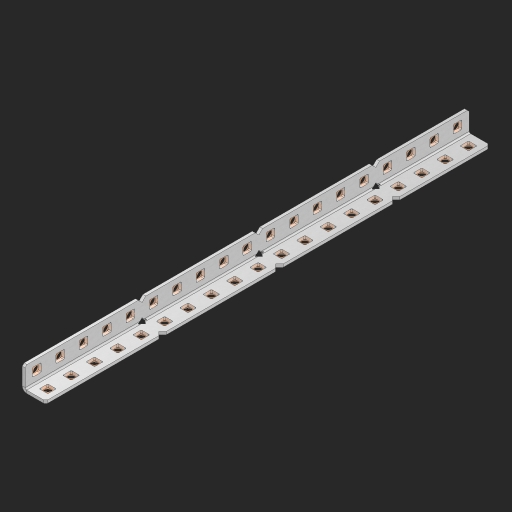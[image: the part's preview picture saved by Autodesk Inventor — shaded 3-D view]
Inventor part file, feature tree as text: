
AUTODESK INVENTOR PART (.ipt)
format: ipt  version: 2023 (Build 270158000, 158)  size: 778,752 bytes
history: native  units: in
note: dims shown in document units (in); Inventor stores cm internally (conversion verified against a paired STEP export)
features: other x44, extrude x39, sheet_metal_op x8, sketch x5, pattern_linear x1, mirror x1, chamfer x1
ambient origin geometry x8: Origin, YZ Plane, XZ Plane, XY Plane, X Axis, Y Axis, Z Axis, Center Point
bodies: Solid1 (feature_tree), Body (feature_tree)
feature tree (99):
  sheet_metal_op  "Flanges"
  sheet_metal_op  "Body Pattern"
  other  "Arc Length"
  pattern_linear  "Notch Pattern"  Spacing1=0.125in  [1 undecoded]
  other  "Diagonal Plane"
  mirror  "Everything Mirrored"
  chamfer  "End Chamfer"
  sketch  "Sketch1"  dims[d0=0.5in]
  other  "Plate1"
  sketch  "Sketch2"  dims[d1=9.5in]
  other  "Plate2"
  sheet_metal_op  "Bend1"
  sheet_metal_op  "Corner1"
  sketch  "Sketch8"  dims[d2=0.0625in]
  sketch  "Sketch9"  dims[d3=0.0625in]
  other  "Srf91"
  sheet_metal_op  "Body Pattern Sketch"
  other  "Srf92"
  sketch  "Sketch13"  dims[d4=0.0312in d5=0.125in d6=0.0625in d7=0.5in d8=90.0deg d9=0.0312in d10=0.25in d11=0.0625in d12=0.0625in d49=0.182in d50=0.02in d52=0.25in d53=0.0625in d54=0.0in d55=0.172in d56=1.0in d57=0.0in d85=0.1473in d86=0.1782in d89=0.0625in d90=0.0in d91=0.04in d92=0.0491in d95=2.5in d96=0.04in d97=0.25in d98=45.0deg d123=0.204in d126=0.0491in d127=0.1473in d128=0.08in d129=0.04in d130=2.5in d131=7.4803in d133=0.5in d134=0.3937in d136=1.0in]
  other  "Srf856"
  other  "Srf857"
  other  "Srf858"
  other  "Srf859"
  other  "Srf860"
  other  "Srf861"
  other  "Srf1275"
  other  "Srf1276"
  other  "Srf1278"
  other  "Srf1279"
  other  "Srf1280"
  other  "Srf1281"
  other  "Srf1282"
  other  "Srf1283"
  other  "Srf1383"
  other  "Srf1384"
  other  "Srf1385"
  other  "Srf1386"
  other  "Srf1387"
  other  "Srf1388"
  other  "Srf1389"
  other  "Srf1390"
  other  "Srf1391"
  other  "Srf1392"
  other  "Srf1393"
  other  "Srf1394"
  other  "Srf1475"
  other  "Srf1476"
  other  "Srf1477"
  other  "Srf1478"
  other  "Srf1479"
  other  "Srf1480"
  other  "Srf1481"
  other  "Srf1482"
  other  "Srf1483"
  other  "Srf1484"
  other  "Srf1485"
  other  "Srf1486"
  sheet_metal_op  "Body Stamp"
  sheet_metal_op  "Body Circle"
  sheet_metal_op  "Notch"
  extrude  "ExtrusionSrf92"  Depth=0.0625in
  extrude  "ExtrusionSrf856"  Depth=0.5in TaperAngle=90.0deg
  extrude  "ExtrusionSrf857"  Depth=0.25in
  extrude  "ExtrusionSrf858"  Depth=0.0625in
  extrude  "ExtrusionSrf859"  Depth=0.0625in
  extrude  "ExtrusionSrf860"  Depth=0.3937in
  extrude  "ExtrusionSrf861"  Depth=0.02in
  extrude  "ExtrusionSrf1275"  Depth=0.25in
  extrude  "ExtrusionSrf1276"  Depth=0.0625in
  extrude  "ExtrusionSrf1277"  TaperAngle=0.0deg  [1 undecoded]
  extrude  "ExtrusionSrf1278"  Depth=0.3937in
  extrude  "ExtrusionSrf1279"  Depth=0.3937in TaperAngle=0.0deg
  extrude  "ExtrusionSrf1280"  Depth=0.3937in
  extrude  "ExtrusionSrf1281"  Depth=0.3937in
  extrude  "ExtrusionSrf1282"  Depth=0.0625in
  extrude  "ExtrusionSrf1383"  Depth=0.3937in TaperAngle=0.0deg
  extrude  "ExtrusionSrf1384"  Depth=0.3937in
  extrude  "ExtrusionSrf1385"  Depth=0.25in TaperAngle=45.0deg
  extrude  "ExtrusionSrf1386"  Depth=0.3937in
  extrude  "ExtrusionSrf1387"  Depth=0.3937in
  extrude  "ExtrusionSrf1388"  Depth=0.3937in
  extrude  "ExtrusionSrf1389"  Depth=0.3937in
  extrude  "ExtrusionSrf1390"  Depth=0.3937in
  extrude  "ExtrusionSrf1391"  Depth=0.3937in
  extrude  "ExtrusionSrf1392"  Depth=0.3937in
  extrude  "ExtrusionSrf1393"  Depth=0.5in
  extrude  "ExtrusionSrf1394"  [1 undecoded]
  extrude  "ExtrusionSrf1475"  [1 undecoded]
  extrude  "ExtrusionSrf1476"  [1 undecoded]
  extrude  "ExtrusionSrf1477"  [1 undecoded]
  extrude  "ExtrusionSrf1478"  [1 undecoded]
  extrude  "ExtrusionSrf1479"  [1 undecoded]
  extrude  "ExtrusionSrf1480"  [1 undecoded]
  extrude  "ExtrusionSrf1481"  [1 undecoded]
  extrude  "ExtrusionSrf1482"  [1 undecoded]
  extrude  "ExtrusionSrf1483"  [1 undecoded]
  extrude  "ExtrusionSrf1484"  [1 undecoded]
  extrude  "ExtrusionSrf1485"  [1 undecoded]
  extrude  "ExtrusionSrf1486"  [1 undecoded]
note: 15 required parameter values undecoded (feature->parameter linkage not recoverable at this tier; creation-order binding heuristic only, values carry confidence <= 0.55)
